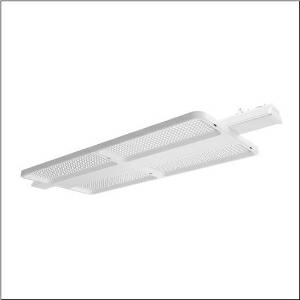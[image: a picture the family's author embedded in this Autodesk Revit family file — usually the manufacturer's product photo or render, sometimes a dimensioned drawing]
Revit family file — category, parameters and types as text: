
# Revit family: highbay_11_fur_licross_r__tragschiene_maxi_51hn11db3tla_240d
name_source: partatom
category: Lighting Fixtures
units: mm (PartAtom-declared; Revit-internal decimal feet)

## family parameters
Cut with Voids When Loaded = No
Host = Face
Light Source = No
Part Type = Normal
Room Calculation Point = No
Round Connector Dimension = Use Diameter
Shared = No

## types (1)
- --- (1 x LED, 53070 lm, 295.1 W, 3000K)
    Apparent Load = 295 VA
    CIE Flux Codes = 85 97 100 100 100
    Color Rendering = 80
    Color Temperature = 3000K
    Default Elevation = 1800 mm
    Description = high bay luminaire Highbay 11 for Licross® trunking rail maxi; direct symmetric narrow distribution, light control with lens of PMMA; UGR ≤ 22 (X = 4H | Y = 8H | S = 0.25H | reflection values 70/50/20); luminous flux: 53.070lm; light colour: 830, colour temperature: 3000K, MacAdam ≤ 2 SDCM (initial), colour rendering: CRI > 80; luminous efficacy: 179,8lm/W; rated service life: 100.000h (L95/B50) at AT= 25°C; control: DALI 2; luminaire connection: plug, 5-pole, with phase selectionmains connection: 230..240V, AC 50/60Hz; connected load: 295,1W; protection rating (complete): IP64; insulation class (complete): insulation class I (protective earthing); protection symbol: D; impact resistance: IK07; certification: CE, ENEC, VDE, UKCA; internal wiring halogen-free; luminaire LABS conformity tested according to VDMA 24364:2018-05; corresponds to IFS (International Featured Standards) requirements for safety and quality in the food industry; housing frame of high-performance plastic PA6, matt traffic white (RAL 9016); cover of PMMA; fixing on rail side of steel, galvanised, white; blank cover of PC/ABS, traffic white (RAL 9016); dimension (LxWxH): 1.250 x 442 x 71mm; permissible operating ambient temperature: -40..+50°C (reducing of maximum allowable ambient temperature of 5°C with ceiling mounting); packaging unit: 1 piece
    Height = 72 mm  [stored 0.23622 ft]
    Lamp = 1 x LED
    Lamp Light Flux = 53070 lm
    Lamp Power = 295.1 W
    Lamp count = 1
    Length = 946 mm
    Luminous efficacy = 180 lm/W
    Manufacturer = Siteco
    ModVariant = No
    Model = 51HN11DB3TLA
    Mounting Place = Ceiling
    Mounting Type = Pendant
    Number of Poles = 1
    OnlyDefault = Yes
    Power Factor = 1
    Product Name = Highbay 11 für Licross® Tragschiene maxi
    Product group = high bay luminaire
    ProductGroupID = 901
    Protection Class = Protection class I
    Protection Degree = IP 64
    RLX_Detail_Level = 1
    RLX_Emergency_Light_Flux = 0 lm
    RLX_Emergency_Type = 0
    RLX_Emergency_Type_DB = No
    RlxData = <blob elided: 24389 chars, md5=bc4d44d0>
    Socket = socket
    Standby Power = 0 W
    System Light Flux = 53071 lm
    System Power = 295 W
    Type Comments = factory setting: luminous flux: 100 % | dim-lin: 254 | 664 mA
    Type Image = l_1361711.jpg
    URL = http://relux.com
    VarID = @adj_004351
    Voltage = 0 V
    Weight = 0.00 kg
    Width = 442 mm

note: [stored X ft] marks values corroborated as IEEE doubles in the binary element streams (Revit-internal decimal feet)

## geometry (parser evidence)
native form markers: Blend x4, Sweep x10
no freeform markers — native parametric forms only
